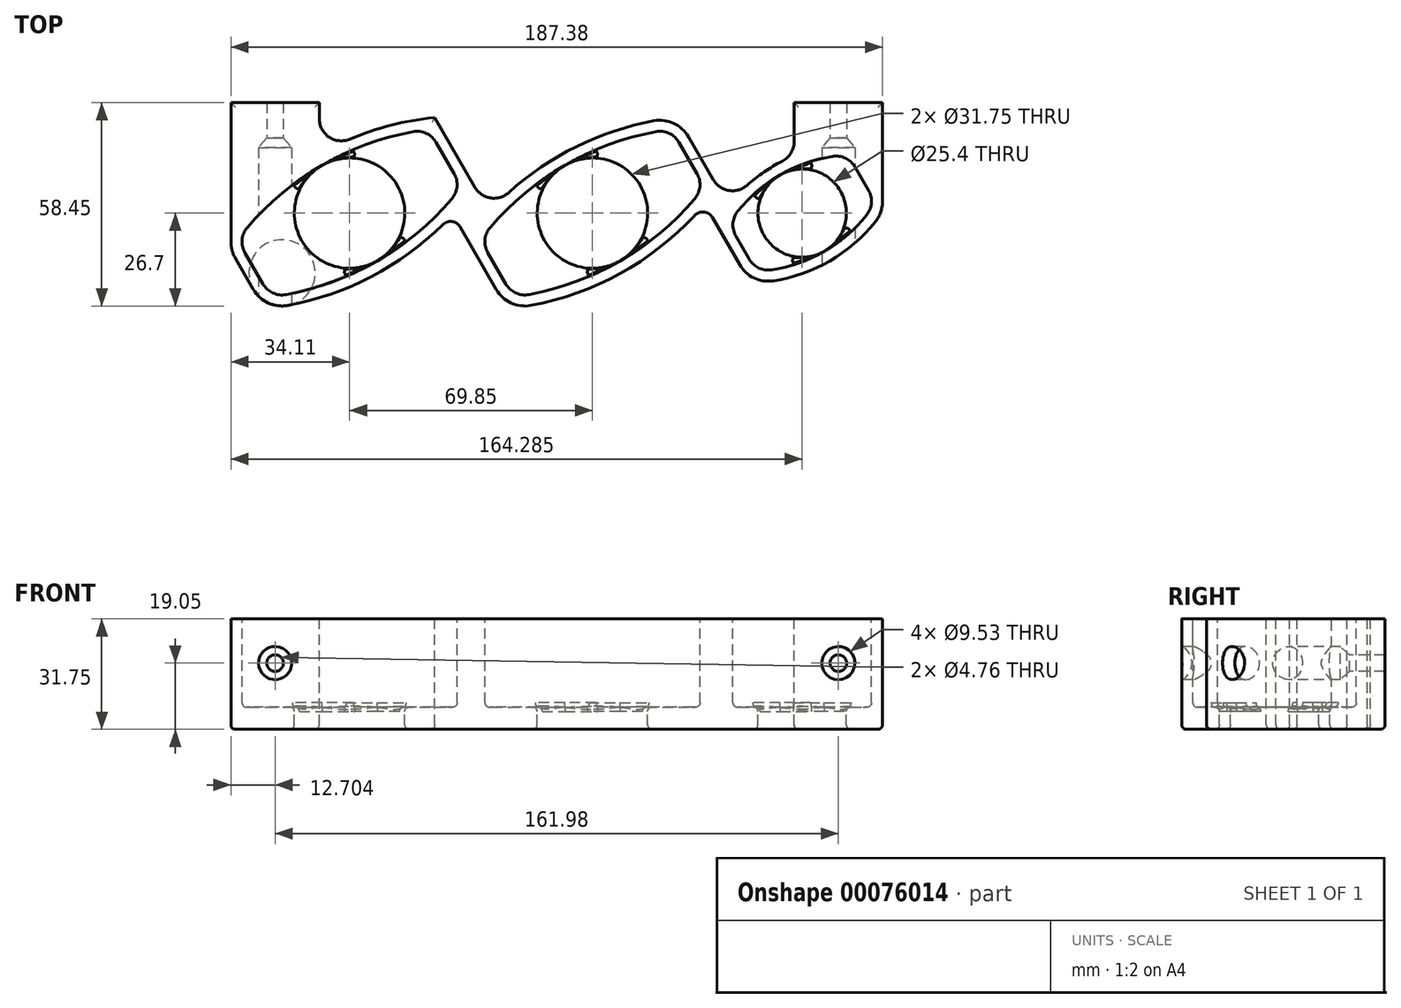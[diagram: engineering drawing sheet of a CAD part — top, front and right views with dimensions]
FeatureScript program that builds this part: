
annotation { "Feature Type Name" : "Feature", "Feature Type Description" : "" }
export const myFeature = defineFeature(function(context is Context, id is Id, definition is map)
    precondition{}
    {
        {
            var Q0;
            Q0=qCreatedBy(makeId("Right.planeOp"),FACE);
            var sketch = newSketch(context, id + "F0", { "sketchPlane" : qUnion([Q0])});
            skLineSegment(sketch, "E0", {"start": v(0, 31.75) * mm, "end": v(0, 0) * mm});
            skLineSegment(sketch, "E1", {"start": v(0, 0) * mm, "end": v(-63.5, 0) * mm});
            skLineSegment(sketch, "E2", {"start": v(-63.5, 0) * mm, "end": v(-63.5, 31.75) * mm});
            skLineSegment(sketch, "E3", {"start": v(-63.5, 31.75) * mm, "end": v(0, 31.75) * mm});
            skSolve(sketch);
        }
        {
            var Q0;
            Q0 = qSketchRegion(id + "F0", true);
            extrude(context, id + "F1", {"entities" : qUnion([Q0]), "depth" : 203.2 * mm, "symmetric" : true});
        }
        {
            var Q0;
            Q0=makeQuery(id+"F1.opExtrude","SWEPT_FACE",FACE,{"disambiguationData":[OSD([sQuery(id+"F0.wireOp",EDGE,"E3")])]});
            var sketch = newSketch(context, id + "F2", { "sketchPlane" : qUnion([Q0])});
            skLineSegment(sketch, "E4", {"start": v(-87.23, -43.15) * mm, "end": v(-82.06, -52.1) * mm});
            skLineSegment(sketch, "E5", {"start": v(-27.07, -20.35) * mm, "end": v(-32.24, -11.4) * mm});
            skLineSegment(sketch, "E6", {"start": v(-65.09, -18) * mm, "end": v(-49.21, -45.5) * mm, "construction": true});
            skPoint(sketch, "E7", {"position": v(-57.15, -31.75) * mm});
            skLineSegment(sketch, "E8", {"start": v(-101.6, -31.75) * mm, "end": v(101.6, -31.75) * mm, "construction": true});
            skArc(sketch, "E9", {"start": v(-38.9, -8.33) * mm, "mid": v(-65.09, -18) * mm, "end": v(-86.56, -35.85) * mm});
            skLineSegment(sketch, "E10", {"start": v(-80.23, -45.08) * mm, "end": v(-29.65, -15.88) * mm, "construction": true});
            skArc(sketch, "E11.MirrorCS", {"start": v(-27.74, -27.65) * mm, "mid": v(-49.21, -45.5) * mm, "end": v(-75.4, -55.17) * mm});
            skPoint(sketch, "E12.newPointB", {"position": v(-89.4, -39.38) * mm});
            skArc(sketch, "E12.filletArc", {"start": v(-86.56, -35.85) * mm, "mid": v(-88.05, -39.4) * mm, "end": v(-87.23, -43.15) * mm});
            skPoint(sketch, "E13.newPointA", {"position": v(-79.88, -55.87) * mm});
            skArc(sketch, "E13.filletArc", {"start": v(-82.06, -52.1) * mm, "mid": v(-79.22, -54.7) * mm, "end": v(-75.4, -55.17) * mm});
            skPoint(sketch, "E14.newPointA", {"position": v(-24.9, -24.12) * mm});
            skArc(sketch, "E14.filletArc", {"start": v(-27.74, -27.65) * mm, "mid": v(-26.25, -24.1) * mm, "end": v(-27.07, -20.35) * mm});
            skPoint(sketch, "E15.newPointB", {"position": v(-34.42, -7.63) * mm});
            skArc(sketch, "E15.filletArc", {"start": v(-32.24, -11.4) * mm, "mid": v(-35.08, -8.8) * mm, "end": v(-38.9, -8.33) * mm});
            skSolve(sketch);
        }
        {
            var Q0;
            Q0 = qSketchRegion(id + "F2", true);
            extrude(context, id + "F3", {"entities" : qUnion([Q0]), "operationType" : NewBodyOperationType.REMOVE, "oppositeDirection" : true, "depth" : 25.4 * mm});
        }
        {
            var Q0;
            Q0=makeQuery(id+"F1.opExtrude","SWEPT_FACE",FACE,{"disambiguationData":[OSD([sQuery(id+"F0.wireOp",EDGE,"E3")])]});
            var sketch = newSketch(context, id + "F4", { "sketchPlane" : qUnion([Q0])});
            skLineSegment(sketch, "E16", {"start": v(-17.38, -43.15) * mm, "end": v(-12.21, -52.1) * mm});
            skLineSegment(sketch, "E17", {"start": v(42.78, -20.35) * mm, "end": v(37.61, -11.4) * mm});
            skLineSegment(sketch, "E18", {"start": v(4.76, -18) * mm, "end": v(20.64, -45.5) * mm, "construction": true});
            skPoint(sketch, "E19", {"position": v(12.7, -31.75) * mm});
            skLineSegment(sketch, "E20", {"start": v(-101.6, -31.75) * mm, "end": v(101.6, -31.75) * mm, "construction": true});
            skArc(sketch, "E21", {"start": v(30.95, -8.33) * mm, "mid": v(4.76, -18) * mm, "end": v(-16.7, -35.85) * mm});
            skLineSegment(sketch, "E22", {"start": v(-10.42, -45.1) * mm, "end": v(40.2, -15.88) * mm, "construction": true});
            skArc(sketch, "E23.MirrorCS", {"start": v(42.1, -27.65) * mm, "mid": v(20.64, -45.5) * mm, "end": v(-5.55, -55.17) * mm});
            skPoint(sketch, "E24.newPointB", {"position": v(-19.56, -39.38) * mm});
            skArc(sketch, "E24.filletArc", {"start": v(-16.7, -35.85) * mm, "mid": v(-18.2, -39.4) * mm, "end": v(-17.38, -43.15) * mm});
            skPoint(sketch, "E25.newPointA", {"position": v(-10.03, -55.87) * mm});
            skArc(sketch, "E25.filletArc", {"start": v(-12.21, -52.1) * mm, "mid": v(-9.37, -54.7) * mm, "end": v(-5.55, -55.17) * mm});
            skPoint(sketch, "E26.newPointA", {"position": v(44.96, -24.12) * mm});
            skArc(sketch, "E26.filletArc", {"start": v(42.1, -27.65) * mm, "mid": v(43.6, -24.1) * mm, "end": v(42.78, -20.35) * mm});
            skPoint(sketch, "E27.newPointB", {"position": v(35.43, -7.63) * mm});
            skArc(sketch, "E27.filletArc", {"start": v(37.61, -11.4) * mm, "mid": v(34.77, -8.8) * mm, "end": v(30.95, -8.33) * mm});
            skPoint(sketch, "E28", {"position": v(-14.8, -47.63) * mm});
            skSolve(sketch);
        }
        {
            var Q0;
            Q0 = qSketchRegion(id + "F4", true);
            extrude(context, id + "F5", {"entities" : qUnion([Q0]), "operationType" : NewBodyOperationType.REMOVE, "oppositeDirection" : true, "depth" : 25.4 * mm});
        }
        {
            var Q0;
            Q0=makeQuery(id+"F1.opExtrude","SWEPT_FACE",FACE,{"disambiguationData":[OSD([sQuery(id+"F0.wireOp",EDGE,"E3")])]});
            var sketch = newSketch(context, id + "F6", { "sketchPlane" : qUnion([Q0])});
            skCircle(sketch, "E29", {"center": v(-57.15, -31.75) * mm, "radius": 15.88 * mm});
            skCircle(sketch, "E30", {"center": v(12.7, -31.75) * mm, "radius": 15.88 * mm});
            skLineSegment(sketch, "E31", {"start": v(4.76, -18) * mm, "end": v(20.64, -45.5) * mm, "construction": true});
            skSolve(sketch);
        }
        {
            var Q0;
            Q0 = qSketchRegion(id + "F6", true);
            var Q1;
            Q1=makeQuery(id+"F1.opExtrude","SWEPT_FACE",FACE,{"disambiguationData":[OSD([sQuery(id+"F0.wireOp",EDGE,"E1")])]});
            extrude(context, id + "F7", {"entities" : qUnion([Q0]), "operationType" : NewBodyOperationType.REMOVE, "endBound" : BoundingType.UP_TO_SURFACE, "oppositeDirection" : true, "endBoundEntityFace" : qUnion([Q1]), "depth" : 25.4 * mm});
        }
        {
            var Q0;
            Q0=makeQuery(id+"F1.opExtrude","SWEPT_FACE",FACE,{"disambiguationData":[OSD([sQuery(id+"F0.wireOp",EDGE,"E3")])]});
            var sketch = newSketch(context, id + "F8", { "sketchPlane" : qUnion([Q0])});
            skCircle(sketch, "E32", {"center": v(73.02, -31.75) * mm, "radius": 12.7 * mm});
            skSolve(sketch);
        }
        {
            var Q0;
            Q0 = qSketchRegion(id + "F8", true);
            extrude(context, id + "F9", {"entities" : qUnion([Q0]), "operationType" : NewBodyOperationType.REMOVE, "endBound" : BoundingType.THROUGH_ALL, "oppositeDirection" : true, "depth" : 25.4 * mm});
        }
        {
            var Q0;
            Q0=makeQuery(id+"F8.imprint","IMPRINT",FACE,{"disambiguationData":[TD([[makeQuery(id+"F8.imprint","IMPRINT",EDGE,{"derivedFrom":sQuery(id+"F8.wireOp",EDGE,"E32")}),-1.0]])]});
            var sketch = newSketch(context, id + "F10", { "sketchPlane" : qUnion([Q0])});
            skLineSegment(sketch, "E33", {"start": v(55.87, -41.66) * mm, "end": v(90.18, -21.84) * mm});
            skLineSegment(sketch, "E34", {"start": v(66.67, -20.75) * mm, "end": v(79.37, -42.75) * mm});
            skLineSegment(sketch, "E35", {"start": v(53.95, -38.34) * mm, "end": v(57.78, -44.97) * mm});
            skLineSegment(sketch, "E36", {"start": v(88.27, -18.53) * mm, "end": v(92.1, -25.16) * mm});
            skArc(sketch, "E37", {"start": v(81.8, -15.43) * mm, "mid": v(66.67, -20.75) * mm, "end": v(54.5, -31.18) * mm});
            skArc(sketch, "E38", {"start": v(64.25, -48.07) * mm, "mid": v(79.37, -42.75) * mm, "end": v(91.55, -32.32) * mm});
            skPoint(sketch, "E39.visualSharp", {"position": v(51.9, -34.78) * mm});
            skArc(sketch, "E39.filletArc", {"start": v(54.5, -31.18) * mm, "mid": v(53.12, -34.68) * mm, "end": v(53.95, -38.34) * mm});
            skPoint(sketch, "E40.visualSharp", {"position": v(59.84, -48.53) * mm});
            skArc(sketch, "E40.filletArc", {"start": v(57.78, -44.97) * mm, "mid": v(60.54, -47.53) * mm, "end": v(64.25, -48.07) * mm});
            skPoint(sketch, "E41.visualSharp", {"position": v(94.15, -28.72) * mm});
            skArc(sketch, "E41.filletArc", {"start": v(91.55, -32.32) * mm, "mid": v(92.93, -28.82) * mm, "end": v(92.1, -25.16) * mm});
            skPoint(sketch, "E42.visualSharp", {"position": v(86.21, -14.97) * mm});
            skArc(sketch, "E42.filletArc", {"start": v(88.27, -18.53) * mm, "mid": v(85.51, -15.97) * mm, "end": v(81.8, -15.43) * mm});
            skSolve(sketch);
        }
        {
            var Q0;
            Q0 = qSketchRegion(id + "F10", true);
            extrude(context, id + "F11", {"entities" : qUnion([Q0]), "operationType" : NewBodyOperationType.REMOVE, "oppositeDirection" : true, "depth" : 25.4 * mm});
        }
        {
            var Q0;
            Q0=makeQuery(id+"F1.opExtrude","SWEPT_FACE",FACE,{"disambiguationData":[OSD([sQuery(id+"F0.wireOp",EDGE,"E3")])]});
            var sketch = newSketch(context, id + "F12", { "sketchPlane" : qUnion([Q0])});
            skArc(sketch, "E43.0", {"start": v(-30.3, -35.06) * mm, "mid": v(-50.83, -50) * mm, "end": v(-74.82, -58.29) * mm});
            skArc(sketch, "E43.1", {"start": v(-84.81, -53.69) * mm, "mid": v(-80.55, -57.58) * mm, "end": v(-74.82, -58.29) * mm});
            skLineSegment(sketch, "E43.2", {"start": v(-89.98, -44.74) * mm, "end": v(-84.81, -53.69) * mm});
            skArc(sketch, "E44.0", {"start": v(42.12, -32.4) * mm, "mid": v(20.65, -49.13) * mm, "end": v(-4.97, -58.29) * mm});
            skArc(sketch, "E44.1", {"start": v(-14.96, -53.69) * mm, "mid": v(-10.7, -57.58) * mm, "end": v(-4.97, -58.29) * mm});
            skLineSegment(sketch, "E44.2", {"start": v(-25.33, -35.73) * mm, "end": v(-14.96, -53.69) * mm});
            skArc(sketch, "E45.0", {"start": v(64.74, -51.21) * mm, "mid": v(80.96, -45.5) * mm, "end": v(94.02, -34.3) * mm});
            skArc(sketch, "E45.1", {"start": v(55.03, -46.56) * mm, "mid": v(59.17, -50.39) * mm, "end": v(64.74, -51.21) * mm});
            skLineSegment(sketch, "E45.2", {"start": v(47.2, -32.98) * mm, "end": v(55.03, -46.56) * mm});
            skPoint(sketch, "E46.visualSharp", {"position": v(-27.43, -32.09) * mm});
            skArc(sketch, "E46.filletArc", {"start": v(-25.33, -35.73) * mm, "mid": v(-27.65, -34.17) * mm, "end": v(-30.3, -35.06) * mm});
            skPoint(sketch, "E47.visualSharp", {"position": v(44.99, -29.16) * mm});
            skArc(sketch, "E47.filletArc", {"start": v(47.2, -32.98) * mm, "mid": v(44.8, -31.41) * mm, "end": v(42.12, -32.4) * mm});
            skLineSegment(sketch, "E48.0", {"start": v(-101.6, -63.5) * mm, "end": v(-101.6, 0) * mm});
            skLineSegment(sketch, "E48.1", {"start": v(101.6, -63.5) * mm, "end": v(-101.6, -63.5) * mm});
            skLineSegment(sketch, "E48.2", {"start": v(101.6, -63.5) * mm, "end": v(101.6, 0) * mm});
            skPoint(sketch, "E49.orphan", {"position": v(101.6, 0) * mm});
            skPoint(sketch, "E50.orphan", {"position": v(-101.6, 0) * mm});
            skArc(sketch, "E51.0", {"start": v(-91.26, -39.98) * mm, "mid": v(-90.93, -42.44) * mm, "end": v(-89.98, -44.74) * mm});
            skLineSegment(sketch, "E52", {"start": v(-91.26, -39.98) * mm, "end": v(-91.26, 0) * mm});
            skLineSegment(sketch, "E53", {"start": v(-91.26, 0) * mm, "end": v(-101.6, 0) * mm});
            skArc(sketch, "E54.0", {"start": v(94.02, -34.3) * mm, "mid": v(95.58, -31.5) * mm, "end": v(96.12, -28.34) * mm});
            skLineSegment(sketch, "E55", {"start": v(96.12, -28.34) * mm, "end": v(96.12, 0) * mm});
            skLineSegment(sketch, "E56", {"start": v(96.12, 0) * mm, "end": v(101.6, 0) * mm});
            skSolve(sketch);
        }
        {
            var Q0;
            Q0 = qSketchRegion(id + "F12", true);
            extrude(context, id + "F13", {"entities" : qUnion([Q0]), "operationType" : NewBodyOperationType.REMOVE, "endBound" : BoundingType.THROUGH_ALL, "oppositeDirection" : true, "depth" : 25.4 * mm});
        }
        {
            var Q0;
            Q0=makeQuery(id+"F1.opExtrude","SWEPT_FACE",FACE,{"disambiguationData":[OSD([sQuery(id+"F0.wireOp",EDGE,"E0")])]});
            var sketch = newSketch(context, id + "F14", { "sketchPlane" : qUnion([Q0])});
            skLineSegment(sketch, "E57", {"start": v(91.26, 31.75) * mm, "end": v(56.56, 31.75) * mm});
            skLineSegment(sketch, "E58", {"start": v(56.56, 31.75) * mm, "end": v(64.8, 46.04) * mm});
            skLineSegment(sketch, "E59", {"start": v(73.06, 50.8) * mm, "end": v(74.76, 50.8) * mm});
            skLineSegment(sketch, "E60", {"start": v(83, 46.04) * mm, "end": v(91.26, 31.75) * mm});
            skLineSegment(sketch, "E61", {"start": v(73.9, 50.8) * mm, "end": v(73.9, 31.75) * mm, "construction": true});
            skCircle(sketch, "E62", {"center": v(73.9, 41.27) * mm, "radius": 2.38 * mm});
            skPoint(sketch, "E63.visualSharp", {"position": v(80.26, 50.8) * mm});
            skArc(sketch, "E63.filletArc", {"start": v(83, 46.04) * mm, "mid": v(79.52, 49.52) * mm, "end": v(74.76, 50.8) * mm});
            skPoint(sketch, "E64.visualSharp", {"position": v(67.56, 50.8) * mm});
            skArc(sketch, "E64.filletArc", {"start": v(73.06, 50.8) * mm, "mid": v(68.3, 49.52) * mm, "end": v(64.8, 46.04) * mm});
            skLineSegment(sketch, "E65", {"start": v(-2.43, 31.75) * mm, "end": v(-2.43, 52.35) * mm, "construction": true});
            skLineSegment(sketch, "E66.MirrorCS", {"start": v(-77.92, 50.8) * mm, "end": v(-79.63, 50.8) * mm});
            skLineSegment(sketch, "E67.MirrorCS", {"start": v(-78.78, 50.8) * mm, "end": v(-78.78, 31.75) * mm, "construction": true});
            skArc(sketch, "E68.MirrorCS", {"start": v(-87.88, 46.04) * mm, "mid": v(-84.39, 49.52) * mm, "end": v(-79.63, 50.8) * mm});
            skArc(sketch, "E69.MirrorCS", {"start": v(-77.92, 50.8) * mm, "mid": v(-73.16, 49.52) * mm, "end": v(-69.68, 46.04) * mm});
            skLineSegment(sketch, "E70.MirrorCS", {"start": v(-96.12, 31.75) * mm, "end": v(-61.43, 31.75) * mm});
            skLineSegment(sketch, "E71.MirrorCS", {"start": v(-61.43, 31.75) * mm, "end": v(-69.68, 46.04) * mm});
            skPoint(sketch, "E72.MirrorP", {"position": v(-85.13, 50.8) * mm});
            skLineSegment(sketch, "E73.MirrorCS", {"start": v(-87.88, 46.04) * mm, "end": v(-96.12, 31.75) * mm});
            skPoint(sketch, "E74.MirrorP", {"position": v(-72.43, 50.8) * mm});
            skCircle(sketch, "E75.MirrorC", {"center": v(-78.78, 41.27) * mm, "radius": 2.38 * mm});
            skSolve(sketch);
        }
        {
            var Q0;
            Q0=qCreatedBy(makeId("Top.planeOp"),FACE);
            cPlane(context, id + "F15", {"entities" : qUnion([Q0]), "cplaneType" : CPlaneType.OFFSET, "offset" : 19.05 * mm, "width" : 152.4 * mm, "height" : 152.4 * mm});
        }
        {
            var Q0;
            Q0=makeQuery(id+"F1.opExtrude","SWEPT_FACE",FACE,{"disambiguationData":[OSD([sQuery(id+"F0.wireOp",EDGE,"E0")])]});
            var sketch = newSketch(context, id + "F16", { "sketchPlane" : qUnion([Q0])});
            skLineSegment(sketch, "E76", {"start": v(-2.43, 0) * mm, "end": v(-2.43, 31.75) * mm, "construction": true});
            skLineSegment(sketch, "E77", {"start": v(-78.63, 15.88) * mm, "end": v(73.77, 15.88) * mm, "construction": true});
            skPoint(sketch, "E78", {"position": v(-96.12, 15.87) * mm});
            skPoint(sketch, "E79", {"position": v(-2.43, 15.88) * mm});
            skCircle(sketch, "E80", {"center": v(73.77, 15.88) * mm, "radius": 1.59 * mm});
            skCircle(sketch, "E81", {"center": v(-2.43, 15.88) * mm, "radius": 1.59 * mm});
            skCircle(sketch, "E82", {"center": v(-78.63, 15.87) * mm, "radius": 1.59 * mm});
            skSolve(sketch);
        }
        {
            var Q0;
            Q0=qCreatedBy(id+"F15.planeOp",FACE);
            var sketch = newSketch(context, id + "F17", { "sketchPlane" : qUnion([Q0])});
            skLineSegment(sketch, "E83", {"start": v(2.43, 0) * mm, "end": v(2.43, -76.2) * mm});
            skLineSegment(sketch, "E84", {"start": v(2.43, -76.2) * mm, "end": v(7.2, -76.2) * mm});
            skLineSegment(sketch, "E85", {"start": v(7.2, -76.2) * mm, "end": v(7.2, -12.9) * mm});
            skLineSegment(sketch, "E86", {"start": v(7.2, -12.9) * mm, "end": v(4.82, -10.16) * mm});
            skLineSegment(sketch, "E87", {"start": v(4.82, -10.16) * mm, "end": v(4.82, 0) * mm});
            skLineSegment(sketch, "E88", {"start": v(2.43, 0) * mm, "end": v(4.82, 0) * mm});
            skSolve(sketch);
        }
        {
            var Q0;
            Q0=qCreatedBy(id+"F15.planeOp",FACE);
            var sketch = newSketch(context, id + "F18", { "sketchPlane" : qUnion([Q0])});
            skLineSegment(sketch, "E89", {"start": v(-78.56, 0) * mm, "end": v(-78.56, -76.2) * mm});
            skLineSegment(sketch, "E90", {"start": v(-78.56, -76.2) * mm, "end": v(-73.8, -76.2) * mm});
            skLineSegment(sketch, "E91", {"start": v(-73.8, -76.2) * mm, "end": v(-73.8, -12.9) * mm});
            skLineSegment(sketch, "E92", {"start": v(-73.8, -12.9) * mm, "end": v(-76.17, -10.16) * mm});
            skLineSegment(sketch, "E93", {"start": v(-76.17, -10.16) * mm, "end": v(-76.17, 0) * mm});
            skLineSegment(sketch, "E94", {"start": v(-76.17, 0) * mm, "end": v(-78.56, 0) * mm});
            skSolve(sketch);
        }
        {
            var Q0;
            Q0 = qSketchRegion(id + "F18", true);
            var Q1;
            Q1=sQuery(id+"F18.wireOp",EDGE,"E89");
            revolve(context, id + "F19", {"operationType" : NewBodyOperationType.REMOVE, "entities" : qUnion([Q0]), "axis" : qUnion([Q1]), "revolveType" : RevolveType.FULL, "oppositeDirection" : true});
        }
        {
            var Q0;
            Q0=qCreatedBy(id+"F15.planeOp",FACE);
            var sketch = newSketch(context, id + "F20", { "sketchPlane" : qUnion([Q0])});
            skLineSegment(sketch, "E95", {"start": v(83.42, 0) * mm, "end": v(83.42, -76.2) * mm});
            skLineSegment(sketch, "E96", {"start": v(83.42, -76.2) * mm, "end": v(88.19, -76.2) * mm});
            skLineSegment(sketch, "E97", {"start": v(88.19, -76.2) * mm, "end": v(88.19, -12.9) * mm});
            skLineSegment(sketch, "E98", {"start": v(88.19, -12.9) * mm, "end": v(85.8, -10.16) * mm});
            skLineSegment(sketch, "E99", {"start": v(85.8, -10.16) * mm, "end": v(85.8, 0) * mm});
            skLineSegment(sketch, "E100", {"start": v(83.42, 0) * mm, "end": v(85.8, 0) * mm});
            skSolve(sketch);
        }
        {
            var Q0;
            Q0 = qSketchRegion(id + "F20", true);
            var Q1;
            Q1=sQuery(id+"F20.wireOp",EDGE,"E95");
            revolve(context, id + "F21", {"operationType" : NewBodyOperationType.REMOVE, "entities" : qUnion([Q0]), "axis" : qUnion([Q1]), "revolveType" : RevolveType.FULL, "oppositeDirection" : true});
        }
        {
            var Q0;
            Q0=makeQuery(id+"F1.opExtrude","SWEPT_FACE",FACE,{"disambiguationData":[OSD([sQuery(id+"F0.wireOp",EDGE,"E3")])]});
            var sketch = newSketch(context, id + "F22", { "sketchPlane" : qUnion([Q0])});
            skArc(sketch, "E101.0", {"start": v(33.72, -4.66) * mm, "mid": v(6.05, -13.67) * mm, "end": v(-17.02, -31.41) * mm});
            skLineSegment(sketch, "E102.0", {"start": v(-17.02, -31.41) * mm, "end": v(-35.15, 0) * mm});
            skPoint(sketch, "E103.orphan", {"position": v(-91.26, 0) * mm});
            skPoint(sketch, "E104.0.start.orphan", {"position": v(96.12, 0) * mm});
            skLineSegment(sketch, "E105", {"start": v(33.72, -4.66) * mm, "end": v(65.8, 0) * mm});
            skLineSegment(sketch, "E106", {"start": v(65.8, 0) * mm, "end": v(-35.15, 0) * mm});
            skSolve(sketch);
        }
        {
            var Q0;
            Q0 = qSketchRegion(id + "F22", true);
            extrude(context, id + "F28", {"entities" : qUnion([Q0]), "operationType" : NewBodyOperationType.REMOVE, "endBound" : BoundingType.THROUGH_ALL, "oppositeDirection" : true, "depth" : 25.4 * mm});
        }
        {
            var Q0;
            Q0=makeQuery(id+"F1.opExtrude","SWEPT_FACE",FACE,{"disambiguationData":[OSD([sQuery(id+"F0.wireOp",EDGE,"E3")])]});
            var sketch = newSketch(context, id + "F23", { "sketchPlane" : qUnion([Q0])});
            skArc(sketch, "E107.0", {"start": v(70.72, -15.23) * mm, "mid": v(60.31, -21.16) * mm, "end": v(51.75, -29.54) * mm});
            skLineSegment(sketch, "E108.0", {"start": v(51.75, -29.54) * mm, "end": v(32.02, 4.64) * mm});
            skLineSegment(sketch, "E109.0", {"start": v(70.72, -15.23) * mm, "end": v(70.72, 27.49) * mm});
            skLineSegment(sketch, "E110.0", {"start": v(96.12, 0) * mm, "end": v(34.7, 0) * mm});
            skPoint(sketch, "E111.orphan", {"position": v(65.8, 0) * mm});
            skSolve(sketch);
        }
        {
            var Q0;
            Q0 = qSketchRegion(id + "F23", true);
            var Q1;
            {var subQ5=sQuery(id+"F23.wireOp",EDGE,"E107.0");Q1=makeQuery(id+"F23.imprint","IMPRINT",FACE,{"disambiguationData":[TD([[makeQuery(id+"F23.imprint","IMPRINT",EDGE,{"derivedFrom":subQ5}),-1.0]])]});}
            extrude(context, id + "F29", {"entities" : qUnion([Q0, Q1]), "operationType" : NewBodyOperationType.REMOVE, "endBound" : BoundingType.THROUGH_ALL, "oppositeDirection" : true, "depth" : 25.4 * mm});
        }
        {
            var Q0;
            Q0=makeQuery(id+"F1.opExtrude","SWEPT_FACE",FACE,{"disambiguationData":[OSD([sQuery(id+"F0.wireOp",EDGE,"E3")])]});
            var sketch = newSketch(context, id + "F24", { "sketchPlane" : qUnion([Q0])});
            skArc(sketch, "E112.0", {"start": v(-11.47, -4.66) * mm, "mid": v(-53.97, -9.25) * mm, "end": v(-88.97, -33.79) * mm});
            skLineSegment(sketch, "E113.0", {"start": v(-65.86, -39.98) * mm, "end": v(-65.86, 23.3) * mm});
            skLineSegment(sketch, "E114.0", {"start": v(-17.02, -31.41) * mm, "end": v(-35.15, 0) * mm});
            skLineSegment(sketch, "E114.1", {"start": v(-35.15, 0) * mm, "end": v(-91.26, 0) * mm});
            skSolve(sketch);
        }
        {
            var Q0;
            Q0 = qSketchRegion(id + "F24", true);
            var Q1;
            {var subQ0=sQuery(id+"F24.wireOp",EDGE,"E113.0");var subQ1=sQuery(id+"F24.wireOp",EDGE,"E112.0");var subQ2=makeQuery(id+"F24.imprint","INTERSECT",VERTEX,{"derivedFrom":[subQ1,subQ0]});Q1=makeQuery(id+"F24.imprint","IMPRINT",FACE,{"disambiguationData":[TD([[makeQuery(id+"F24.imprint","IMPRINT",EDGE,{"disambiguationData":[TD([[subQ2,1.0]])],"derivedFrom":subQ1}),-1.0]])]});}
            extrude(context, id + "F25", {"entities" : qUnion([Q0, Q1]), "operationType" : NewBodyOperationType.REMOVE, "endBound" : BoundingType.THROUGH_ALL, "oppositeDirection" : true, "depth" : 25.4 * mm});
        }
        {
            var Q0;
            Q0=makeQuery(id+"F28.boolean.opBoolean","COPY",EDGE,{"derivedFrom":makeQuery(id+"F28.opExtrude","SWEPT_EDGE",EDGE,{"disambiguationData":[OSD([sQuery(id+"F22.wireOp",EDGE,"E101.0"),sQuery(id+"F22.wireOp",EDGE,"E102.0")])]})});
            var Q1;
            Q1=makeQuery(id+"F29.boolean.opBoolean","COPY",EDGE,{"derivedFrom":makeQuery(id+"F29.opExtrude","SWEPT_EDGE",EDGE,{"disambiguationData":[OSD([sQuery(id+"F23.wireOp",EDGE,"E107.0"),sQuery(id+"F23.wireOp",EDGE,"E108.0")])]})});
            var Q2;
            Q2=makeQuery(id+"F29.boolean.opBoolean","COPY",EDGE,{"derivedFrom":makeQuery(id+"F29.opExtrude","SWEPT_EDGE",EDGE,{"disambiguationData":[OSD([sQuery(id+"F23.wireOp",EDGE,"E107.0"),sQuery(id+"F23.wireOp",EDGE,"E109.0")])]})});
            var Q3;
            Q3=makeQuery(id+"F25.boolean.opBoolean","COPY",EDGE,{"derivedFrom":makeQuery(id+"F25.opExtrude","SWEPT_EDGE",EDGE,{"disambiguationData":[OSD([sQuery(id+"F24.wireOp",EDGE,"E112.0"),sQuery(id+"F24.wireOp",EDGE,"E113.0")])]})});
            fillet(context, id + "F30", {"entities" : qUnion([Q0, Q1, Q2, Q3]), "radius" : 6.35 * mm, "tangentPropagation" : true, "allowEdgeOverflow" : false});
        }
        {
            var Q0;
            Q0=makeQuery(id+"F29.boolean.opBoolean","INTERSECT",EDGE,{"derivedFrom":[makeQuery(id+"F28.boolean.opBoolean","COPY",FACE,{"derivedFrom":makeQuery(id+"F28.opExtrude","SWEPT_FACE",FACE,{"disambiguationData":[OSD([sQuery(id+"F22.wireOp",EDGE,"E105")])]})}),makeQuery(id+"F29.opExtrude","SWEPT_FACE",FACE,{"disambiguationData":[OSD([sQuery(id+"F23.wireOp",EDGE,"E108.0")])]})]});
            var Q1;
            Q1=makeQuery(id+"F25.boolean.opBoolean","COPY",EDGE,{"derivedFrom":makeQuery(id+"F25.opExtrude","SWEPT_EDGE",EDGE,{"disambiguationData":[OSD([sQuery(id+"F24.wireOp",EDGE,"E112.0"),sQuery(id+"F24.wireOp",EDGE,"E114.0")])]})});
            fillet(context, id + "F26", {"entities" : qUnion([Q0, Q1]), "radius" : 9.52 * mm, "tangentPropagation" : true, "allowEdgeOverflow" : false});
        }
        {
            var Q0;
            Q0=makeQuery(id+"F13.boolean.opBoolean","COPY",EDGE,{"derivedFrom":makeQuery(id+"F13.opExtrude","CAP_EDGE",EDGE,{"disambiguationData":[OSD([sQuery(id+"F12.wireOp",EDGE,"E44.0")])],"isStart":true})});
            var Q1;
            Q1=makeQuery(id+"F28.boolean.opBoolean","COPY",EDGE,{"derivedFrom":makeQuery(id+"F28.opExtrude","CAP_EDGE",EDGE,{"disambiguationData":[OSD([sQuery(id+"F22.wireOp",EDGE,"E101.0")])],"isStart":true})});
            var Q2;
            Q2=makeQuery(id+"F3.boolean.opBoolean","COPY",EDGE,{"derivedFrom":makeQuery(id+"F3.opExtrude","CAP_EDGE",EDGE,{"disambiguationData":[OSD([sQuery(id+"F2.wireOp",EDGE,"E9")])],"isStart":true})});
            var Q3;
            Q3=makeQuery(id+"F25.boolean.opBoolean","COPY",EDGE,{"derivedFrom":makeQuery(id+"F25.opExtrude","CAP_EDGE",EDGE,{"disambiguationData":[OSD([sQuery(id+"F24.wireOp",EDGE,"E113.0")])],"isStart":true})});
            var Q4;
            Q4=makeQuery(id+"F13.boolean.opBoolean","INTERSECT",EDGE,{"derivedFrom":[makeQuery(id+"F1.opExtrude","SWEPT_FACE",FACE,{"disambiguationData":[OSD([sQuery(id+"F0.wireOp",EDGE,"E1")])]}),makeQuery(id+"F13.opExtrude","SWEPT_FACE",FACE,{"disambiguationData":[OSD([sQuery(id+"F12.wireOp",EDGE,"E44.0")])]})]});
            var Q5;
            Q5=makeQuery(id+"F28.boolean.opBoolean","INTERSECT",EDGE,{"derivedFrom":[makeQuery(id+"F1.opExtrude","SWEPT_FACE",FACE,{"disambiguationData":[OSD([sQuery(id+"F0.wireOp",EDGE,"E1")])]}),makeQuery(id+"F28.opExtrude","SWEPT_FACE",FACE,{"disambiguationData":[OSD([sQuery(id+"F22.wireOp",EDGE,"E101.0")])]})]});
            var Q6;
            Q6=makeQuery(id+"F25.boolean.opBoolean","INTERSECT",EDGE,{"derivedFrom":[makeQuery(id+"F1.opExtrude","SWEPT_FACE",FACE,{"disambiguationData":[OSD([sQuery(id+"F0.wireOp",EDGE,"E1")])]}),makeQuery(id+"F25.opExtrude","SWEPT_FACE",FACE,{"disambiguationData":[OSD([sQuery(id+"F24.wireOp",EDGE,"E113.0")])]})]});
            var Q7;
            {var subQ0=sQuery(id+"F2.wireOp",EDGE,"E15.filletArc");var subQ1=sQuery(id+"F2.wireOp",EDGE,"E9");Q7=makeQuery(id+"F7.boolean.opBoolean","SPLIT",EDGE,{"disambiguationData":[TD([makeQuery(id+"F3.boolean.opBoolean","COPY",FACE,{"derivedFrom":makeQuery(id+"F3.opExtrude","SWEPT_FACE",FACE,{"disambiguationData":[OSD([subQ0])]})})])],"derivedFrom":makeQuery(id+"F3.boolean.opBoolean","COPY",EDGE,{"derivedFrom":makeQuery(id+"F3.opExtrude","CAP_EDGE",EDGE,{"disambiguationData":[OSD([subQ1])],"isStart":false})})});}
            var Q8;
            Q8=makeQuery(id+"F7.boolean.opBoolean","COPY",FACE,{"derivedFrom":makeQuery(id+"F7.opExtrude","SWEPT_FACE",FACE,{"disambiguationData":[OSD([sQuery(id+"F6.wireOp",EDGE,"E29")])]})});
            var Q9;
            Q9=makeQuery(id+"F7.boolean.opBoolean","INTERSECT",EDGE,{"disambiguationData":[OD(0.0)],"derivedFrom":[makeQuery(id+"F3.boolean.opBoolean","COPY",FACE,{"derivedFrom":makeQuery(id+"F3.opExtrude","CAP_FACE",FACE,{"disambiguationData":[OSD([sQuery(id+"F2.wireOp",EDGE,"E4"),sQuery(id+"F2.wireOp",EDGE,"E5"),sQuery(id+"F2.wireOp",EDGE,"E9"),sQuery(id+"F2.wireOp",EDGE,"E11.MirrorCS"),sQuery(id+"F2.wireOp",EDGE,"E12.filletArc"),sQuery(id+"F2.wireOp",EDGE,"E13.filletArc"),sQuery(id+"F2.wireOp",EDGE,"E14.filletArc"),sQuery(id+"F2.wireOp",EDGE,"E15.filletArc")])],"isStart":false})}),makeQuery(id+"F7.opExtrude","SWEPT_FACE",FACE,{"disambiguationData":[OSD([sQuery(id+"F6.wireOp",EDGE,"E29")])]})]});
            var Q10;
            {var subQ0=sQuery(id+"F2.wireOp",EDGE,"E13.filletArc");var subQ1=sQuery(id+"F2.wireOp",EDGE,"E11.MirrorCS");Q10=makeQuery(id+"F7.boolean.opBoolean","SPLIT",EDGE,{"disambiguationData":[TD([makeQuery(id+"F3.boolean.opBoolean","COPY",FACE,{"derivedFrom":makeQuery(id+"F3.opExtrude","SWEPT_FACE",FACE,{"disambiguationData":[OSD([subQ0])]})})])],"derivedFrom":makeQuery(id+"F3.boolean.opBoolean","COPY",EDGE,{"derivedFrom":makeQuery(id+"F3.opExtrude","CAP_EDGE",EDGE,{"disambiguationData":[OSD([subQ1])],"isStart":false})})});}
            var Q11;
            Q11=makeQuery(id+"F7.boolean.opBoolean","INTERSECT",EDGE,{"disambiguationData":[OD(0.0)],"derivedFrom":[makeQuery(id+"F5.boolean.opBoolean","COPY",FACE,{"derivedFrom":makeQuery(id+"F5.opExtrude","CAP_FACE",FACE,{"disambiguationData":[OSD([sQuery(id+"F4.wireOp",EDGE,"E16"),sQuery(id+"F4.wireOp",EDGE,"E17"),sQuery(id+"F4.wireOp",EDGE,"E21"),sQuery(id+"F4.wireOp",EDGE,"E23.MirrorCS"),sQuery(id+"F4.wireOp",EDGE,"E24.filletArc"),sQuery(id+"F4.wireOp",EDGE,"E25.filletArc"),sQuery(id+"F4.wireOp",EDGE,"E26.filletArc"),sQuery(id+"F4.wireOp",EDGE,"E27.filletArc")])],"isStart":false})}),makeQuery(id+"F7.opExtrude","SWEPT_FACE",FACE,{"disambiguationData":[OSD([sQuery(id+"F6.wireOp",EDGE,"E30")])]})]});
            var Q12;
            Q12=makeQuery(id+"F1.opExtrude","SWEPT_FACE",FACE,{"disambiguationData":[OSD([sQuery(id+"F0.wireOp",EDGE,"E1")])]});
            var Q13;
            {var subQ0=sQuery(id+"F4.wireOp",EDGE,"E26.filletArc");var subQ1=sQuery(id+"F4.wireOp",EDGE,"E23.MirrorCS");Q13=makeQuery(id+"F7.boolean.opBoolean","SPLIT",EDGE,{"disambiguationData":[TD([makeQuery(id+"F5.boolean.opBoolean","COPY",FACE,{"derivedFrom":makeQuery(id+"F5.opExtrude","SWEPT_FACE",FACE,{"disambiguationData":[OSD([subQ0])]})})])],"derivedFrom":makeQuery(id+"F5.boolean.opBoolean","COPY",EDGE,{"derivedFrom":makeQuery(id+"F5.opExtrude","CAP_EDGE",EDGE,{"disambiguationData":[OSD([subQ1])],"isStart":false})})});}
            var Q14;
            {var subQ0=sQuery(id+"F4.wireOp",EDGE,"E25.filletArc");var subQ1=sQuery(id+"F4.wireOp",EDGE,"E23.MirrorCS");Q14=makeQuery(id+"F7.boolean.opBoolean","SPLIT",EDGE,{"disambiguationData":[TD([makeQuery(id+"F5.boolean.opBoolean","COPY",FACE,{"derivedFrom":makeQuery(id+"F5.opExtrude","SWEPT_FACE",FACE,{"disambiguationData":[OSD([subQ0])]})})])],"derivedFrom":makeQuery(id+"F5.boolean.opBoolean","COPY",EDGE,{"derivedFrom":makeQuery(id+"F5.opExtrude","CAP_EDGE",EDGE,{"disambiguationData":[OSD([subQ1])],"isStart":false})})});}
            var Q15;
            Q15=makeQuery(id+"F11.boolean.opBoolean","INTERSECT",EDGE,{"disambiguationData":[OD(1.0)],"derivedFrom":[makeQuery(id+"F9.boolean.opBoolean","COPY",FACE,{"derivedFrom":makeQuery(id+"F9.opExtrude","SWEPT_FACE",FACE,{"disambiguationData":[OSD([sQuery(id+"F8.wireOp",EDGE,"E32")])]})}),makeQuery(id+"F11.opExtrude","CAP_FACE",FACE,{"disambiguationData":[OSD([sQuery(id+"F10.wireOp",EDGE,"E35"),sQuery(id+"F10.wireOp",EDGE,"E36"),sQuery(id+"F10.wireOp",EDGE,"E37"),sQuery(id+"F10.wireOp",EDGE,"E38"),sQuery(id+"F10.wireOp",EDGE,"E39.filletArc"),sQuery(id+"F10.wireOp",EDGE,"E40.filletArc"),sQuery(id+"F10.wireOp",EDGE,"E41.filletArc"),sQuery(id+"F10.wireOp",EDGE,"E42.filletArc")])],"isStart":false})]});
            var Q16;
            Q16=makeQuery(id+"F11.boolean.opBoolean","COPY",EDGE,{"derivedFrom":makeQuery(id+"F11.opExtrude","CAP_EDGE",EDGE,{"disambiguationData":[OSD([sQuery(id+"F10.wireOp",EDGE,"E36")])],"isStart":false})});
            var Q17;
            Q17=makeQuery(id+"F11.boolean.opBoolean","INTERSECT",EDGE,{"disambiguationData":[OD(0.0)],"derivedFrom":[makeQuery(id+"F9.boolean.opBoolean","COPY",FACE,{"derivedFrom":makeQuery(id+"F9.opExtrude","SWEPT_FACE",FACE,{"disambiguationData":[OSD([sQuery(id+"F8.wireOp",EDGE,"E32")])]})}),makeQuery(id+"F11.opExtrude","CAP_FACE",FACE,{"disambiguationData":[OSD([sQuery(id+"F10.wireOp",EDGE,"E35"),sQuery(id+"F10.wireOp",EDGE,"E36"),sQuery(id+"F10.wireOp",EDGE,"E37"),sQuery(id+"F10.wireOp",EDGE,"E38"),sQuery(id+"F10.wireOp",EDGE,"E39.filletArc"),sQuery(id+"F10.wireOp",EDGE,"E40.filletArc"),sQuery(id+"F10.wireOp",EDGE,"E41.filletArc"),sQuery(id+"F10.wireOp",EDGE,"E42.filletArc")])],"isStart":false})]});
            var Q18;
            Q18=makeQuery(id+"F11.boolean.opBoolean","COPY",EDGE,{"derivedFrom":makeQuery(id+"F11.opExtrude","CAP_EDGE",EDGE,{"disambiguationData":[OSD([sQuery(id+"F10.wireOp",EDGE,"E35")])],"isStart":false})});
            var Q19;
            Q19=makeQuery(id+"F11.boolean.opBoolean","COPY",EDGE,{"derivedFrom":makeQuery(id+"F11.opExtrude","CAP_EDGE",EDGE,{"disambiguationData":[OSD([sQuery(id+"F10.wireOp",EDGE,"E37")])],"isStart":true})});
            var Q20;
            Q20=makeQuery(id+"F5.boolean.opBoolean","COPY",EDGE,{"derivedFrom":makeQuery(id+"F5.opExtrude","CAP_EDGE",EDGE,{"disambiguationData":[OSD([sQuery(id+"F4.wireOp",EDGE,"E21")])],"isStart":true})});
            fillet(context, id + "F27", {"entities" : qUnion([Q0, Q1, Q2, Q3, Q4, Q5, Q6, Q7, Q8, Q9, Q10, Q11, Q12, Q13, Q14, Q15, Q16, Q17, Q18, Q19, Q20]), "radius" : 1.27 * mm, "tangentPropagation" : true, "allowEdgeOverflow" : false});
        }
    });
